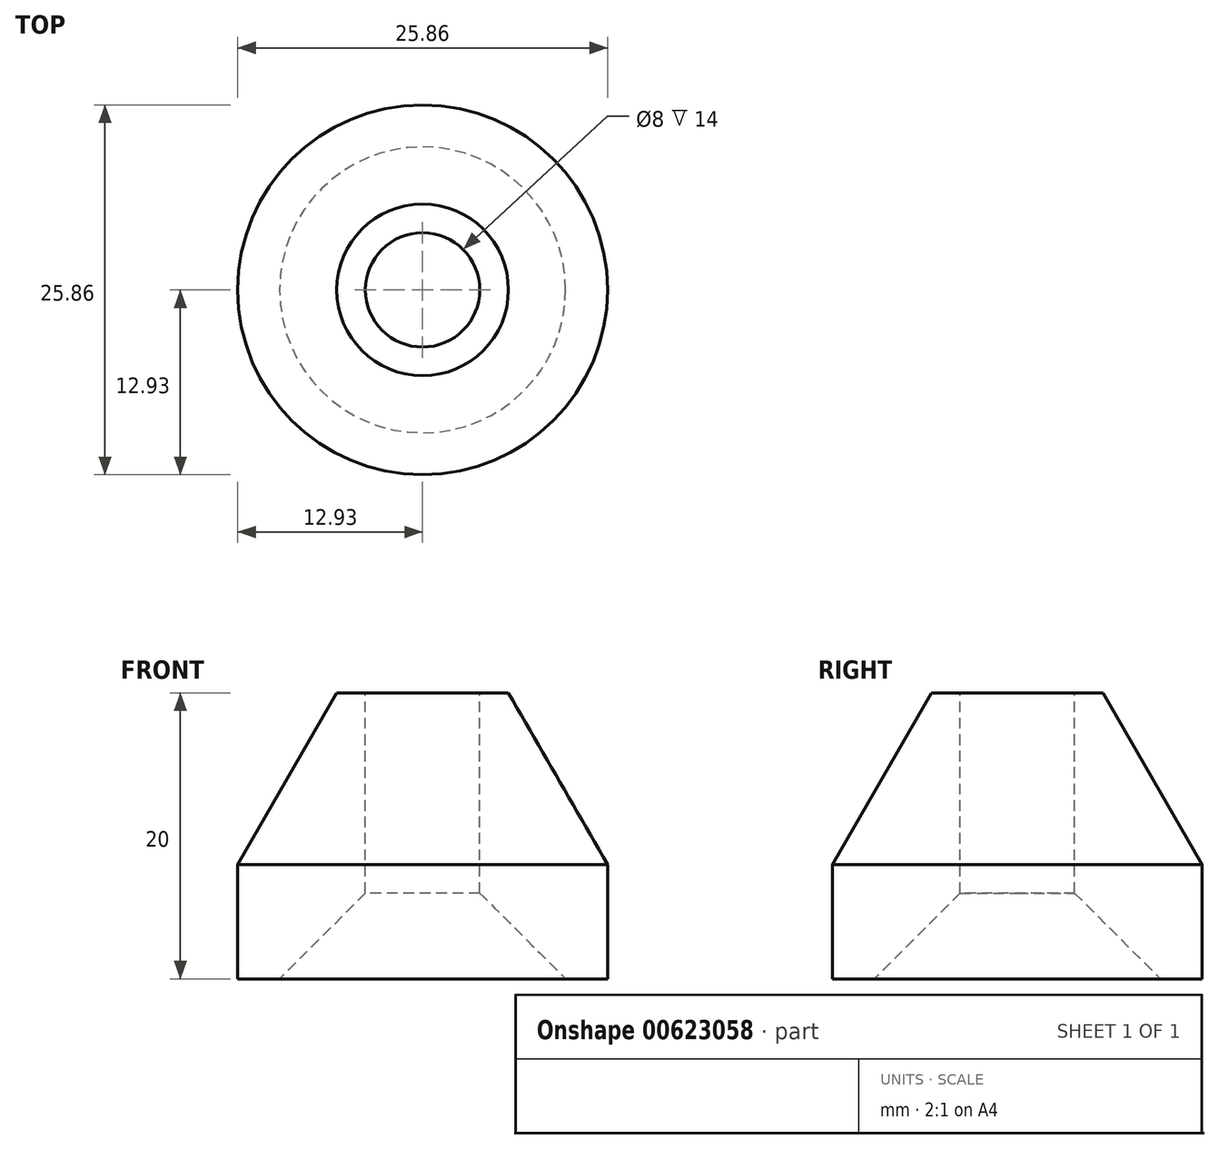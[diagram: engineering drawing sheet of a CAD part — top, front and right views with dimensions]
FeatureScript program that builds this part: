
annotation { "Feature Type Name" : "Feature", "Feature Type Description" : "" }
export const myFeature = defineFeature(function(context is Context, id is Id, definition is map)
    precondition{}
    {
        {
            var Q0;
            Q0=qCreatedBy(makeId("Front.planeOp"),FACE);
            var sketch = newSketch(context, id + "F0", { "sketchPlane" : qUnion([Q0])});
            skLineSegment(sketch, "E0", {"start": v(-10, 0) * mm, "end": v(-12.93, 0) * mm});
            skLineSegment(sketch, "E1", {"start": v(-12.93, 0) * mm, "end": v(-12.93, 8) * mm});
            skLineSegment(sketch, "E2", {"start": v(-12.93, 8) * mm, "end": v(-6, 20) * mm});
            skLineSegment(sketch, "E3", {"start": v(-6, 20) * mm, "end": v(-4, 20) * mm});
            skLineSegment(sketch, "E4", {"start": v(0, 20) * mm, "end": v(0, 0) * mm, "construction": true});
            skLineSegment(sketch, "E5", {"start": v(-4, 6) * mm, "end": v(-4, 20) * mm});
            skLineSegment(sketch, "E6", {"start": v(-10, 0) * mm, "end": v(-4, 6) * mm});
            skPoint(sketch, "E7.orphan", {"position": v(-4, 0) * mm});
            skSolve(sketch);
        }
        {
            var Q0;
            Q0=makeQuery(id+"F0.imprint","IMPRINT",FACE,{"disambiguationData":[TD([[makeQuery(id+"F0.imprint","IMPRINT",EDGE,{"derivedFrom":sQuery(id+"F0.wireOp",EDGE,"E0")}),-1.0]])]});
            var Q1;
            Q1=sQuery(id+"F0.wireOp",EDGE,"E4");
            revolve(context, id + "F1", {"entities" : qUnion([Q0]), "axis" : qUnion([Q1]), "revolveType" : RevolveType.FULL});
        }
    });
